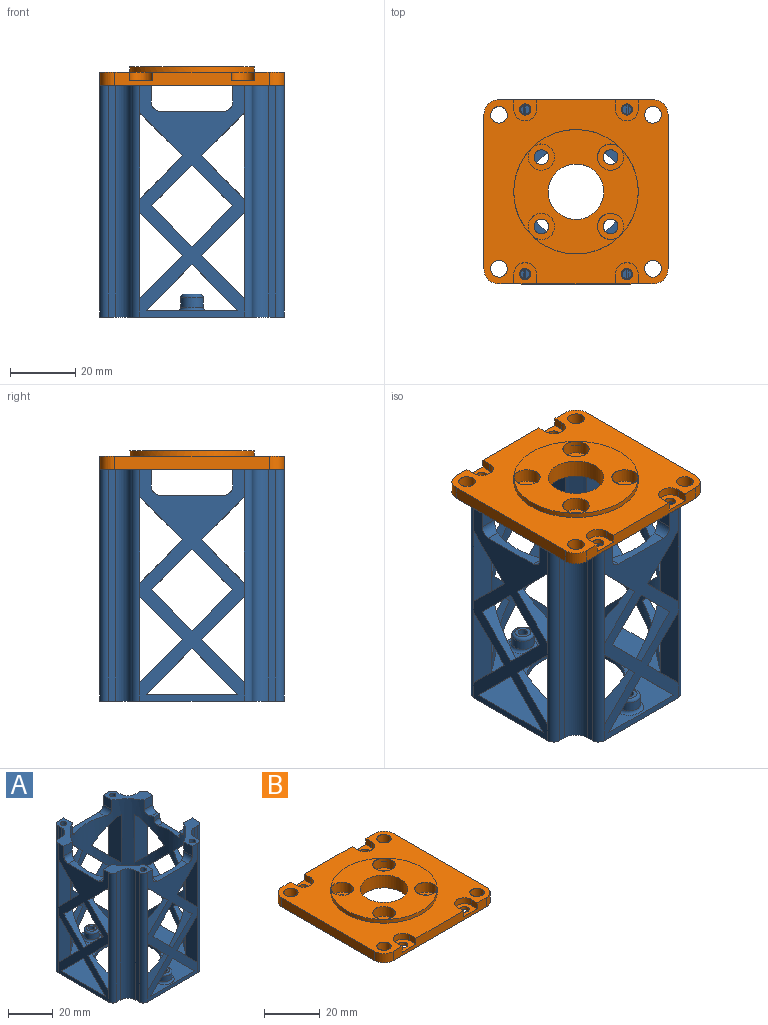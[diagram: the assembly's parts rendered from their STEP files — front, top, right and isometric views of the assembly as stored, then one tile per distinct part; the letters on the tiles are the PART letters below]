
ASSEMBLY  parts=2 mates=1
PART A: 184 faces, bbox 57.2x59.2x71.8 mm
  f0: cylinder r=26mm len=69mm, axis (0,0,-1), area 5201.7mm2, adj f1,f5,f7,f11,f13,f14,f37,f38
  f1: plane 15.7x15.7mm, normal (0,0,1), area 86.9mm2, adj f0,f2,f6,f22,f23,f24,f25,f26
  f2: plane 71x32.15mm, normal (0,-1,0), area 879.2mm2, adj f1,f11,f26,f27,f40,f41,f116,f118
  f3: plane 2.84x1.34mm, normal (0,0,1), area 2.9mm2, adj f120,f166
  f4: plane 2.67x0.93mm, normal (0,0,1), area 1.8mm2, adj f117,f175
  f5: plane 15.7x15.7mm, normal (0,0,1), area 86.9mm2, adj f0,f6,f8,f17,f18,f19,f20,f21
  f6: plane 71x32.15mm, normal (-1,0,0), area 879.2mm2, adj f1,f5,f21,f22,f40,f41,f93,f94
  f7: plane 15.7x15.7mm, normal (0,0,1), area 86.9mm2, adj f0,f8,f12,f32,f33,f34,f35,f36
  f8: plane 71x32.15mm, normal (0,1,0), area 879.2mm2, adj f5,f7,f17,f36,f40,f41,f70,f72
  f9: plane 2.84x1.34mm, normal (0,0,1), area 2.9mm2, adj f74,f148
  f10: plane 2.67x0.93mm, normal (0,0,1), area 1.8mm2, adj f71,f157
  f11: plane 15.7x15.7mm, normal (0,0,1), area 86.9mm2, adj f0,f2,f12,f27,f28,f29,f30,f31
  f12: plane 71x32.15mm, normal (1,0,0), area 816.9mm2, adj f7,f11,f13,f14,f31,f32,f37,f38
  f13: plane 3.46x2mm, normal (0,1,0), area 6.9mm2, adj f0,f12,f38,f51
  f14: plane 3.46x2mm, normal (0,-1,0), area 6.9mm2, adj f0,f12,f39,f46
  f15: cylinder r=1.44mm len=7mm, axis (0,0,-1), area 63.1mm2, adj f41,f179
  f16: cylinder r=1.44mm len=7mm, axis (0,0,-1), area 63.1mm2, adj f41,f177
  f17: cylinder r=2.5mm len=71mm, axis (0,0,-1), area 278.8mm2, adj f5,f8,f18,f41,f71,f90
  f18: plane 71x2.13mm, normal (-1,0,0), area 151mm2, adj f5,f17,f19,f41
  f19: cylinder r=5mm len=71mm, axis (0,0,-1), area 557.6mm2, adj f5,f18,f20,f41
  f20: plane 71x2.13mm, normal (0,1,0), area 151mm2, adj f5,f19,f21,f41
  f21: cylinder r=2.5mm len=71mm, axis (0,0,-1), area 278.8mm2, adj f5,f6,f20,f41,f107,f113
  f22: cylinder r=2.5mm len=71mm, axis (0,0,-1), area 278.8mm2, adj f1,f6,f23,f41,f104,f110
  f23: plane 71x2.13mm, normal (0,-1,0), area 151mm2, adj f1,f22,f24,f41
  f24: cylinder r=5mm len=71mm, axis (0,0,-1), area 557.6mm2, adj f1,f23,f25,f41
  f25: plane 71x2.13mm, normal (-1,0,0), area 151mm2, adj f1,f24,f26,f41
  f26: cylinder r=2.5mm len=71mm, axis (0,0,-1), area 278.8mm2, adj f1,f2,f25,f41,f121,f133
  f27: cylinder r=2.5mm len=71mm, axis (0,0,-1), area 278.8mm2, adj f2,f11,f28,f41,f117,f136
  f28: plane 71x2.13mm, normal (1,0,0), area 151mm2, adj f11,f27,f29,f41
  f29: cylinder r=5mm len=71mm, axis (0,0,-1), area 557.6mm2, adj f11,f28,f30,f41
  f30: plane 71x2.13mm, normal (0,-1,0), area 151mm2, adj f11,f29,f31,f41
  f31: cylinder r=2.5mm len=71mm, axis (0,0,-1), area 278.8mm2, adj f11,f12,f30,f41,f61,f67
  f32: cylinder r=2.5mm len=71mm, axis (0,0,-1), area 278.8mm2, adj f7,f12,f33,f41,f58,f64
  f33: plane 71x2.13mm, normal (0,1,0), area 151mm2, adj f7,f32,f34,f41
  f34: cylinder r=5mm len=71mm, axis (0,0,-1), area 557.6mm2, adj f7,f33,f35,f41
  f35: plane 71x2.13mm, normal (1,0,0), area 151mm2, adj f7,f34,f36,f41
  f36: cylinder r=2.5mm len=71mm, axis (0,0,-1), area 278.8mm2, adj f7,f8,f35,f41,f75,f87
  f37: plane 12x2.9mm, normal (0,0,1), area 29.2mm2, adj f0,f12,f38,f39
  f38: cylinder r=2mm len=3.46mm, axis (-1,0,0), area 10mm2, adj f0,f12,f13,f37
  f39: cylinder r=2mm len=3.46mm, axis (-1,0,0), area 10mm2, adj f0,f12,f14,f37
  f40: plane 56.4x56.4mm, normal (0,0,1), area 1688.5mm2, adj f0,f2,f6,f8,f12,f56,f57,f85
  f41: plane 56.4x56.4mm, normal (0,0,-1), area 2101.2mm2, adj f2,f6,f8,f12,f15,f16,f17,f18
  f42: plane 2.67x0.93mm, normal (0,0,1), area 1.8mm2, adj f121,f166
  f43: plane 2.84x1.34mm, normal (0,0,1), area 2.9mm2, adj f118,f175
  f44: plane 2.67x0.93mm, normal (0,0,1), area 1.8mm2, adj f75,f148
  f45: plane 2.84x1.34mm, normal (0,0,1), area 2.9mm2, adj f72,f157
  f46: plane 4.06x1.65mm, normal (0,0,1), area 6.2mm2, adj f0,f12,f14,f47
  f47: cylinder r=2.85mm len=5.4mm, axis (1,0,0), area 21.2mm2, adj f0,f12,f46,f48
  f48: plane 5.4x5.15mm, normal (0,-1,0), area 27.8mm2, adj f0,f7,f12,f47
  f49: plane 5.4x5.15mm, normal (0,1,0), area 27.8mm2, adj f0,f11,f12,f50
  f50: cylinder r=2.85mm len=5.4mm, axis (1,0,0), area 21.2mm2, adj f0,f12,f49,f51
  f51: plane 4.06x1.65mm, normal (0,0,1), area 6.2mm2, adj f0,f12,f13,f50
  f52: plane 12.82x12.82mm, normal (0,-0.71,-0.71), area 56.6mm2, adj f0,f12,f53,f55
  f53: plane 12.82x12.82mm, normal (0,0.71,-0.71), area 56.6mm2, adj f0,f12,f52,f54
  f54: plane 12.82x12.82mm, normal (0,0.71,0.71), area 56.6mm2, adj f0,f12,f53,f55
  f55: plane 12.82x12.82mm, normal (0,-0.71,0.71), area 56.6mm2, adj f0,f12,f52,f54
  f56: plane 14.63x14.63mm, normal (0,-0.71,-0.71), area 69.9mm2, adj f0,f12,f40,f57
  f57: plane 14.63x14.63mm, normal (0,0.71,-0.71), area 69.9mm2, adj f0,f12,f40,f56
  f58: plane 26.49x7.76mm, normal (0,-1,0), area 205.6mm2, adj f0,f32,f59,f60
  f59: plane 14.01x14.01mm, normal (0,0.71,-0.71), area 81.2mm2, adj f0,f12,f58,f60
  f60: plane 14.01x14.01mm, normal (0,0.71,0.71), area 81.2mm2, adj f0,f12,f58,f59
  f61: plane 26.49x7.76mm, normal (0,1,0), area 205.6mm2, adj f0,f31,f62,f63
  f62: plane 14.01x14.01mm, normal (0,-0.71,0.71), area 81.2mm2, adj f0,f12,f61,f63
  f63: plane 14.01x14.01mm, normal (0,-0.71,-0.71), area 81.2mm2, adj f0,f12,f61,f62
  f64: plane 26.49x7.76mm, normal (0,-1,0), area 205.6mm2, adj f0,f32,f65,f66
  f65: plane 14.01x14.01mm, normal (0,0.71,-0.71), area 81.2mm2, adj f0,f12,f64,f66
  f66: plane 14.01x14.01mm, normal (0,0.71,0.71), area 81.2mm2, adj f0,f12,f64,f65
  f67: plane 26.49x7.76mm, normal (0,1,0), area 205.6mm2, adj f0,f31,f68,f69
  f68: plane 14.01x14.01mm, normal (0,-0.71,-0.71), area 81.2mm2, adj f0,f12,f67,f69
  f69: plane 14.01x14.01mm, normal (0,-0.71,0.71), area 81.2mm2, adj f0,f12,f67,f68
  f70: plane 14.01x14.01mm, normal (-0.71,0,0.71), area 81.2mm2, adj f0,f8,f71,f72
  f71: plane 26.49x7.76mm, normal (1,0,0), area 203.4mm2, adj f0,f10,f17,f70,f72,f149,f153,f154
  f72: plane 14.01x14.01mm, normal (-0.71,0,-0.71), area 77.9mm2, adj f0,f8,f45,f70,f71,f150,f151,f152
  f73: plane 14.01x14.01mm, normal (0.71,0,0.71), area 81.2mm2, adj f0,f8,f74,f75
  f74: plane 14.01x14.01mm, normal (0.71,0,-0.71), area 77.9mm2, adj f0,f8,f9,f73,f75,f140,f144,f145
  f75: plane 26.49x7.76mm, normal (-1,0,0), area 203.4mm2, adj f0,f36,f44,f73,f74,f141,f142,f143
  f76: plane 5.4x5.15mm, normal (1,0,0), area 27.8mm2, adj f0,f5,f8,f80
  f77: plane 5.4x5.15mm, normal (-1,0,0), area 27.8mm2, adj f0,f7,f8,f78
  f78: cylinder r=2.85mm len=5.4mm, axis (0,1,0), area 21.2mm2, adj f0,f8,f77,f79
  f79: plane 19.29x4.06mm, normal (0,0,1), area 54.2mm2, adj f0,f8,f78,f80
  f80: cylinder r=2.85mm len=5.4mm, axis (0,1,0), area 21.2mm2, adj f0,f8,f76,f79
  f81: plane 12.82x12.82mm, normal (0.71,0,-0.71), area 56.6mm2, adj f0,f8,f82,f84
  f82: plane 12.82x12.82mm, normal (-0.71,0,-0.71), area 56.6mm2, adj f0,f8,f81,f83
  f83: plane 12.82x12.82mm, normal (-0.71,0,0.71), area 56.6mm2, adj f0,f8,f82,f84
  f84: plane 12.82x12.82mm, normal (0.71,0,0.71), area 56.6mm2, adj f0,f8,f81,f83
  f85: plane 14.63x14.63mm, normal (0.71,0,-0.71), area 69.9mm2, adj f0,f8,f40,f86
  f86: plane 14.63x14.63mm, normal (-0.71,0,-0.71), area 69.9mm2, adj f0,f8,f40,f85
  f87: plane 26.49x7.76mm, normal (-1,0,0), area 205.6mm2, adj f0,f36,f88,f89
  f88: plane 14.01x14.01mm, normal (0.71,0,0.71), area 81.2mm2, adj f0,f8,f87,f89
  f89: plane 14.01x14.01mm, normal (0.71,0,-0.71), area 81.2mm2, adj f0,f8,f87,f88
  f90: plane 26.49x7.76mm, normal (1,0,0), area 205.6mm2, adj f0,f17,f91,f92
  f91: plane 14.01x14.01mm, normal (-0.71,0,-0.71), area 81.2mm2, adj f0,f8,f90,f92
  f92: plane 14.01x14.01mm, normal (-0.71,0,0.71), area 81.2mm2, adj f0,f8,f90,f91
  f93: plane 5.4x5.15mm, normal (0,1,0), area 27.8mm2, adj f0,f1,f6,f97
  f94: plane 5.4x5.15mm, normal (0,-1,0), area 27.8mm2, adj f0,f5,f6,f95
  f95: cylinder r=2.85mm len=5.4mm, axis (-1,0,0), area 21.2mm2, adj f0,f6,f94,f96
  f96: plane 19.29x4.06mm, normal (0,0,1), area 54.2mm2, adj f0,f6,f95,f97
  f97: cylinder r=2.85mm len=5.4mm, axis (-1,0,0), area 21.2mm2, adj f0,f6,f93,f96
  f98: plane 12.82x12.82mm, normal (0,0.71,-0.71), area 56.6mm2, adj f0,f6,f99,f101
  f99: plane 12.82x12.82mm, normal (0,-0.71,-0.71), area 56.6mm2, adj f0,f6,f98,f100
  f100: plane 12.82x12.82mm, normal (0,-0.71,0.71), area 56.6mm2, adj f0,f6,f99,f101
  f101: plane 12.82x12.82mm, normal (0,0.71,0.71), area 56.6mm2, adj f0,f6,f98,f100
  f102: plane 14.63x14.63mm, normal (0,0.71,-0.71), area 69.9mm2, adj f0,f6,f40,f103
  f103: plane 14.63x14.63mm, normal (0,-0.71,-0.71), area 69.9mm2, adj f0,f6,f40,f102
  f104: plane 26.49x7.76mm, normal (0,1,0), area 205.6mm2, adj f0,f22,f105,f106
  f105: plane 14.01x14.01mm, normal (0,-0.71,-0.71), area 81.2mm2, adj f0,f6,f104,f106
  f106: plane 14.01x14.01mm, normal (0,-0.71,0.71), area 81.2mm2, adj f0,f6,f104,f105
  f107: plane 26.49x7.76mm, normal (0,-1,0), area 205.6mm2, adj f0,f21,f108,f109
  f108: plane 14.01x14.01mm, normal (0,0.71,0.71), area 81.2mm2, adj f0,f6,f107,f109
  f109: plane 14.01x14.01mm, normal (0,0.71,-0.71), area 81.2mm2, adj f0,f6,f107,f108
  f110: plane 26.49x7.76mm, normal (0,1,0), area 205.6mm2, adj f0,f22,f111,f112
  f111: plane 14.01x14.01mm, normal (0,-0.71,-0.71), area 81.2mm2, adj f0,f6,f110,f112
  f112: plane 14.01x14.01mm, normal (0,-0.71,0.71), area 81.2mm2, adj f0,f6,f110,f111
  f113: plane 26.49x7.76mm, normal (0,-1,0), area 205.6mm2, adj f0,f21,f114,f115
  f114: plane 14.01x14.01mm, normal (0,0.71,-0.71), area 81.2mm2, adj f0,f6,f113,f115
  f115: plane 14.01x14.01mm, normal (0,0.71,0.71), area 81.2mm2, adj f0,f6,f113,f114
  f116: plane 14.01x14.01mm, normal (0.71,0,0.71), area 81.2mm2, adj f0,f2,f117,f118
  f117: plane 26.49x7.76mm, normal (-1,0,0), area 203.4mm2, adj f0,f4,f27,f116,f118,f167,f171,f172
  f118: plane 14.01x14.01mm, normal (0.71,0,-0.71), area 77.9mm2, adj f0,f2,f43,f116,f117,f168,f169,f170
  f119: plane 14.01x14.01mm, normal (-0.71,0,0.71), area 81.2mm2, adj f0,f2,f120,f121
  f120: plane 14.01x14.01mm, normal (-0.71,0,-0.71), area 77.9mm2, adj f0,f2,f3,f119,f121,f158,f162,f163
  f121: plane 26.49x7.76mm, normal (1,0,0), area 203.4mm2, adj f0,f26,f42,f119,f120,f159,f160,f161
  f122: plane 5.4x5.15mm, normal (-1,0,0), area 27.8mm2, adj f0,f2,f11,f126
  f123: plane 5.4x5.15mm, normal (1,0,0), area 27.8mm2, adj f0,f1,f2,f124
  f124: cylinder r=2.85mm len=5.4mm, axis (0,-1,0), area 21.2mm2, adj f0,f2,f123,f125
  f125: plane 19.29x4.06mm, normal (0,0,1), area 54.2mm2, adj f0,f2,f124,f126
  f126: cylinder r=2.85mm len=5.4mm, axis (0,-1,0), area 21.2mm2, adj f0,f2,f122,f125
  f127: plane 12.82x12.82mm, normal (-0.71,0,-0.71), area 56.6mm2, adj f0,f2,f128,f130
  f128: plane 12.82x12.82mm, normal (0.71,0,-0.71), area 56.6mm2, adj f0,f2,f127,f129
  f129: plane 12.82x12.82mm, normal (0.71,0,0.71), area 56.6mm2, adj f0,f2,f128,f130
  f130: plane 12.82x12.82mm, normal (-0.71,0,0.71), area 56.6mm2, adj f0,f2,f127,f129
  f131: plane 14.63x14.63mm, normal (-0.71,0,-0.71), area 69.9mm2, adj f0,f2,f40,f132
  f132: plane 14.63x14.63mm, normal (0.71,0,-0.71), area 69.9mm2, adj f0,f2,f40,f131
  f133: plane 26.49x7.76mm, normal (1,0,0), area 205.6mm2, adj f0,f26,f134,f135
  f134: plane 14.01x14.01mm, normal (-0.71,0,0.71), area 81.2mm2, adj f0,f2,f133,f135
  f135: plane 14.01x14.01mm, normal (-0.71,0,-0.71), area 81.2mm2, adj f0,f2,f133,f134
  f136: plane 26.49x7.76mm, normal (-1,0,0), area 205.6mm2, adj f0,f27,f137,f138
  f137: plane 14.01x14.01mm, normal (0.71,0,-0.71), area 81.2mm2, adj f0,f2,f136,f138
  f138: plane 14.01x14.01mm, normal (0.71,0,0.71), area 81.2mm2, adj f0,f2,f136,f137
  f139: cylinder r=15mm len=30mm, axis (0,0,-1), area 188.5mm2, adj f40,f41
  f140: plane 0.58x0.03mm, normal (0,0,-1), area 0mm2, adj f74,f144,f148
  f141: plane 0.6x0.14mm, normal (0,0,-1), area 0mm2, adj f75,f143,f148
  f142: plane 0.6x0.14mm, normal (0,0,-1), area 0mm2, adj f75,f147,f148
  f143: plane 0.59x0.56mm, normal (-0.97,-0.25,0), area 0.3mm2, adj f75,f141,f144,f148
  f144: bspline ~4x4mm, area 0.4mm2, adj f74,f140,f143,f148
  f145: plane 0.58x0.03mm, normal (0,0,-1), area 0mm2, adj f74,f146,f148
  f146: bspline ~4x4mm, area 0.4mm2, adj f74,f145,f147,f148
  f147: plane 0.59x0.56mm, normal (-0.97,0.25,0), area 0.3mm2, adj f75,f142,f146,f148
  f148: cylinder r=1.43mm len=9mm, axis (0,0,1), area 80.3mm2, adj f7,f9,f44,f140,f141,f142,f143,f144
  f149: plane 0.6x0.14mm, normal (0,0,-1), area 0mm2, adj f71,f153,f157
  f150: plane 0.58x0.03mm, normal (0,0,-1), area 0mm2, adj f72,f152,f157
  f151: plane 0.58x0.03mm, normal (0,0,-1), area 0mm2, adj f72,f156,f157
  f152: bspline ~4x4mm, area 0.4mm2, adj f72,f150,f153,f157
  f153: plane 0.59x0.56mm, normal (0.97,-0.25,0), area 0.3mm2, adj f71,f149,f152,f157
  f154: plane 0.6x0.14mm, normal (0,0,-1), area 0mm2, adj f71,f155,f157
  f155: plane 0.59x0.56mm, normal (0.97,0.25,0), area 0.3mm2, adj f71,f154,f156,f157
  f156: bspline ~4x4mm, area 0.4mm2, adj f72,f151,f155,f157
  f157: cylinder r=1.43mm len=9mm, axis (0,0,1), area 80.3mm2, adj f5,f10,f45,f149,f150,f151,f152,f153
  f158: plane 0.58x0.03mm, normal (0,0,-1), area 0mm2, adj f120,f162,f166
  f159: plane 0.6x0.14mm, normal (0,0,-1), area 0mm2, adj f121,f161,f166
  f160: plane 0.6x0.14mm, normal (0,0,-1), area 0mm2, adj f121,f165,f166
  f161: plane 0.59x0.56mm, normal (0.97,0.25,0), area 0.3mm2, adj f121,f159,f162,f166
  f162: bspline ~4x4mm, area 0.4mm2, adj f120,f158,f161,f166
  f163: plane 0.58x0.03mm, normal (0,0,-1), area 0mm2, adj f120,f164,f166
  f164: bspline ~4x4mm, area 0.4mm2, adj f120,f163,f165,f166
  f165: plane 0.59x0.56mm, normal (0.97,-0.25,0), area 0.3mm2, adj f121,f160,f164,f166
  f166: cylinder r=1.43mm len=9mm, axis (0,0,1), area 80.3mm2, adj f1,f3,f42,f158,f159,f160,f161,f162
  f167: plane 0.6x0.14mm, normal (0,0,-1), area 0mm2, adj f117,f171,f175
  f168: plane 0.58x0.03mm, normal (0,0,-1), area 0mm2, adj f118,f170,f175
  f169: plane 0.58x0.03mm, normal (0,0,-1), area 0mm2, adj f118,f174,f175
  f170: bspline ~4x4mm, area 0.4mm2, adj f118,f168,f171,f175
  f171: plane 0.59x0.56mm, normal (-0.97,0.25,0), area 0.3mm2, adj f117,f167,f170,f175
  f172: plane 0.6x0.14mm, normal (0,0,-1), area 0mm2, adj f117,f173,f175
  f173: plane 0.59x0.56mm, normal (-0.97,-0.25,0), area 0.3mm2, adj f117,f172,f174,f175
  f174: bspline ~4x4mm, area 0.4mm2, adj f118,f169,f173,f175
  f175: cylinder r=1.43mm len=9mm, axis (0,0,1), area 80.3mm2, adj f4,f11,f43,f167,f168,f169,f170,f171
  f176: cylinder r=3.44mm len=6.87mm, axis (0,0,-1), area 64.7mm2, adj f181,f183
  f177: plane 4.87x4.87mm, normal (0,0,1), area 12.2mm2, adj f16,f183
  f178: cylinder r=3.44mm len=6.87mm, axis (0,0,-1), area 64.7mm2, adj f180,f182
  f179: plane 4.87x4.87mm, normal (0,0,1), area 12.2mm2, adj f15,f182
  f180: torus R=4.43mm, axis (0,0,-1), area 37.5mm2, adj f40,f178
  f181: torus R=4.43mm, axis (0,0,-1), area 37.5mm2, adj f40,f176
  f182: torus R=2.44mm, axis (0,0,1), area 30.3mm2, adj f178,f179
  f183: torus R=2.44mm, axis (0,0,1), area 30.3mm2, adj f176,f177
PART B: 53 faces, bbox 56.4x56.4x5.6 mm
  f0: cylinder r=1.7mm len=3.4mm, axis (0,0,1), area 15mm2, adj f31,f44
  f1: cylinder r=1.7mm len=3.4mm, axis (0,0,1), area 15mm2, adj f31,f43
  f2: cylinder r=1.7mm len=3.4mm, axis (0,0,1), area 15mm2, adj f31,f42
  f3: cylinder r=1.7mm len=3.4mm, axis (0,0,1), area 15mm2, adj f31,f41
  f4: cylinder r=2.55mm len=5.1mm, axis (0,0,1), area 64.1mm2, adj f22,f31
  f5: cylinder r=2.55mm len=5.1mm, axis (0,0,1), area 64.1mm2, adj f22,f31
  f6: cylinder r=2.55mm len=5.1mm, axis (0,0,1), area 64.1mm2, adj f22,f31
  f7: cone r=4.03mm half-angle=45deg, axis (0,0,1), area 0.9mm2, adj f8,f32
  f8: cylinder r=4mm len=8mm, axis (0,0,1), area 106.2mm2, adj f7,f36
  f9: cylinder r=2.25mm len=4.5mm, axis (0,0,1), area 19.1mm2, adj f31,f36
  f10: cone r=4.03mm half-angle=45deg, axis (0,0,1), area 0.9mm2, adj f11,f32
  f11: cylinder r=4mm len=8mm, axis (0,0,1), area 106.2mm2, adj f10,f35
  f12: cylinder r=2.25mm len=4.5mm, axis (0,0,1), area 19.1mm2, adj f31,f35
  f13: cone r=4.03mm half-angle=45deg, axis (0,0,1), area 0.9mm2, adj f14,f32
  f14: cylinder r=4mm len=8mm, axis (0,0,1), area 106.2mm2, adj f13,f34
  f15: cylinder r=2.25mm len=4.5mm, axis (0,0,1), area 19.1mm2, adj f31,f34
  f16: cylinder r=2.55mm len=5.1mm, axis (0,0,1), area 64.1mm2, adj f22,f31
  f17: cone r=4.03mm half-angle=45deg, axis (0,0,1), area 0.9mm2, adj f18,f32
  f18: cylinder r=4mm len=8mm, axis (0,0,1), area 106.2mm2, adj f17,f33
  f19: cylinder r=2.25mm len=4.5mm, axis (0,0,1), area 19.1mm2, adj f31,f33
  f20: cylinder r=8.5mm len=17mm, axis (0,0,1), area 299.1mm2, adj f31,f32
  f21: cylinder r=19.05mm len=38.1mm, axis (0,0,-1), area 191.5mm2, adj f22,f32
  f22: plane 56.4x56.4mm, normal (0,0,1), area 1780mm2, adj f4,f5,f6,f16,f21,f23,f24,f25
  f23: plane 47.2x4mm, normal (0,-1,0), area 152.4mm2, adj f22,f31,f38,f39,f43,f44,f49,f50
  f24: cylinder r=3.5mm len=7mm, axis (0,0,1), area 28.6mm2, adj f22,f44,f51,f52
  f25: cylinder r=3.5mm len=7mm, axis (0,0,1), area 28.6mm2, adj f22,f43,f49,f50
  f26: plane 47.2x4mm, normal (0,1,0), area 152.4mm2, adj f22,f31,f37,f40,f41,f42,f45,f46
  f27: cylinder r=3.5mm len=7mm, axis (0,0,1), area 28.6mm2, adj f22,f42,f47,f48
  f28: cylinder r=3.5mm len=7mm, axis (0,0,1), area 28.6mm2, adj f22,f41,f45,f46
  f29: plane 47.2x4mm, normal (1,0,0), area 188.8mm2, adj f22,f31,f39,f40
  f30: plane 47.2x4mm, normal (-1,0,0), area 188.8mm2, adj f22,f31,f37,f38
  f31: plane 56.4x56.4mm, normal (0,0,-1), area 2754.2mm2, adj f0,f1,f2,f3,f4,f5,f6,f9
  f32: plane 38.1x38.1mm, normal (0,0,1), area 709.5mm2, adj f7,f10,f13,f17,f20,f21
  f33: plane 8x8mm, normal (0,0,1), area 34.4mm2, adj f18,f19
  f34: plane 8x8mm, normal (0,0,1), area 34.4mm2, adj f14,f15
  f35: plane 8x8mm, normal (0,0,1), area 34.4mm2, adj f11,f12
  f36: plane 8x8mm, normal (0,0,1), area 34.4mm2, adj f8,f9
  f37: cylinder r=4.6mm len=4.6mm, axis (0,0,-1), area 28.9mm2, adj f22,f26,f30,f31
  f38: cylinder r=4.6mm len=4.6mm, axis (0,0,-1), area 28.9mm2, adj f22,f23,f30,f31
  f39: cylinder r=4.6mm len=4.6mm, axis (0,0,-1), area 28.9mm2, adj f22,f23,f29,f31
  f40: cylinder r=4.6mm len=4.6mm, axis (0,0,-1), area 28.9mm2, adj f22,f26,f29,f31
  f41: plane 7x6.5mm, normal (0,0,1), area 31.2mm2, adj f3,f26,f28,f45,f46
  f42: plane 7x6.5mm, normal (0,0,1), area 31.2mm2, adj f2,f26,f27,f47,f48
  f43: plane 7x6.5mm, normal (0,0,1), area 31.2mm2, adj f1,f23,f25,f49,f50
  f44: plane 7x6.5mm, normal (0,0,1), area 31.2mm2, adj f0,f23,f24,f51,f52
  f45: plane 3x2.6mm, normal (1,0,0), area 7.8mm2, adj f22,f26,f28,f41
  f46: plane 3x2.6mm, normal (-1,0,0), area 7.8mm2, adj f22,f26,f28,f41
  f47: plane 3x2.6mm, normal (1,0,0), area 7.8mm2, adj f22,f26,f27,f42
  f48: plane 3x2.6mm, normal (-1,0,0), area 7.8mm2, adj f22,f26,f27,f42
  f49: plane 3x2.6mm, normal (-1,0,0), area 7.8mm2, adj f22,f23,f25,f43
  f50: plane 3x2.6mm, normal (1,0,0), area 7.8mm2, adj f22,f23,f25,f43
  f51: plane 3x2.6mm, normal (-1,0,0), area 7.8mm2, adj f22,f23,f24,f44
  f52: plane 3x2.6mm, normal (1,0,0), area 7.8mm2, adj f22,f23,f24,f44
PLACE A t=(0,0,-34.5)mm
PLACE B at identity fixed
MATE fastened A.f157 <-> B.f3  axis (0,0,1) through (-15.57,25.2,0)mm
